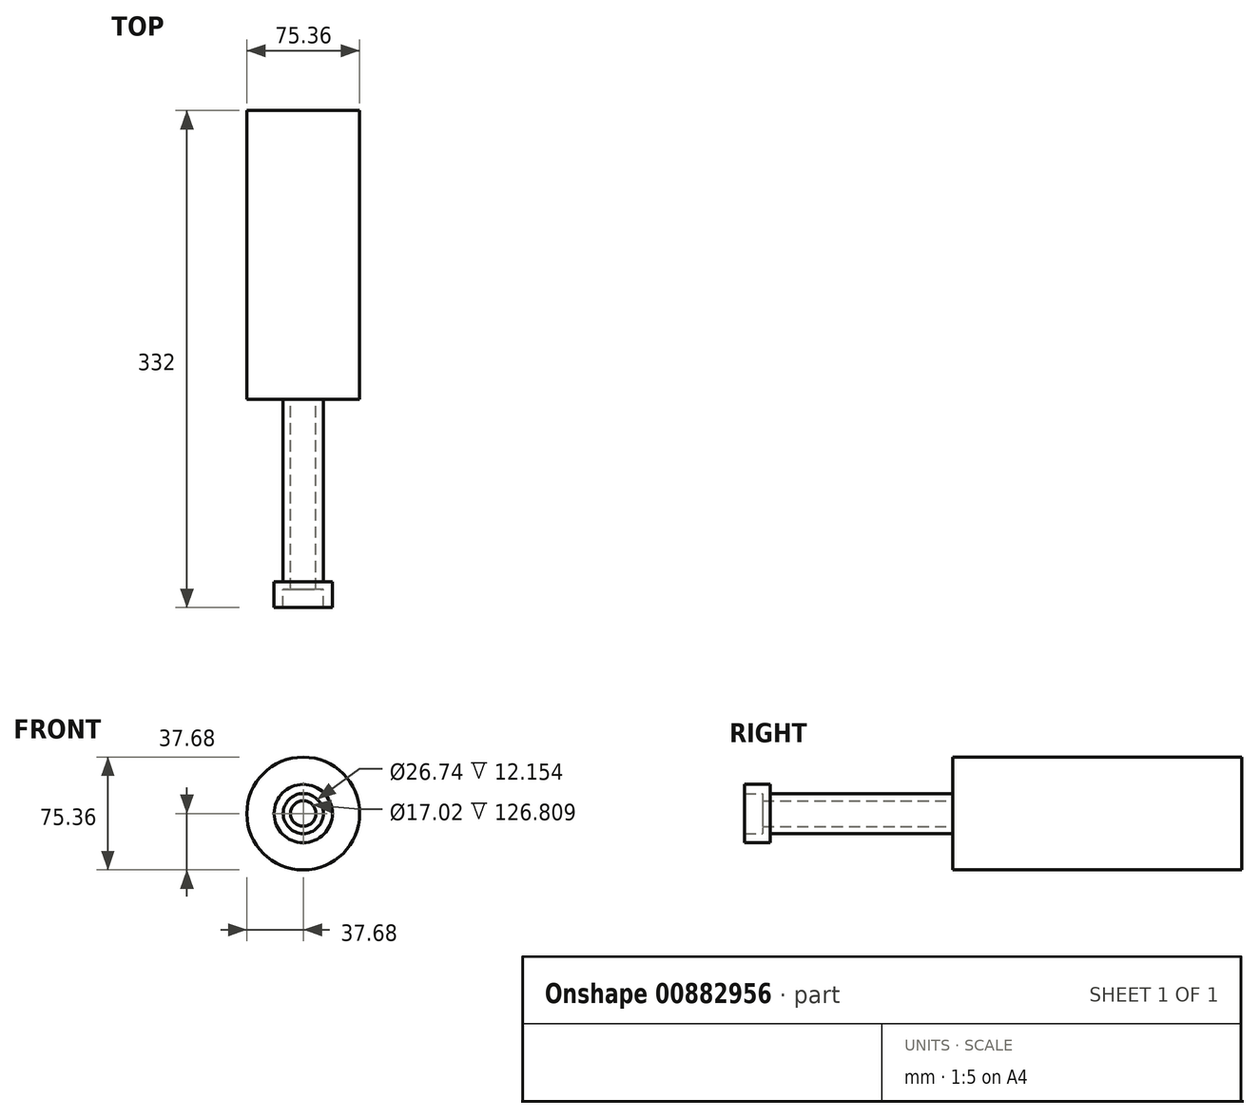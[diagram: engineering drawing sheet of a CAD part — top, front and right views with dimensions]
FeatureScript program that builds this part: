
annotation { "Feature Type Name" : "Feature", "Feature Type Description" : "" }
export const myFeature = defineFeature(function(context is Context, id is Id, definition is map)
    precondition{}
    {
        {
            var Q0;
            Q0=qCreatedBy(makeId("Right.planeOp"),FACE);
            var sketch = newSketch(context, id + "F0", { "sketchPlane" : qUnion([Q0])});
            skLineSegment(sketch, "E0.bottom", {"start": v(0, 37.68) * mm, "end": v(-193.04, 37.68) * mm});
            skLineSegment(sketch, "E0.top", {"start": v(0, 0) * mm, "end": v(-193.04, 0) * mm});
            skLineSegment(sketch, "E0.left", {"start": v(0, 37.68) * mm, "end": v(0, 0) * mm});
            skLineSegment(sketch, "E0.right", {"start": v(-193.04, 37.68) * mm, "end": v(-193.04, 0) * mm});
            skLineSegment(sketch, "E1.bottom", {"start": v(-193.04, 13.37) * mm, "end": v(-314.98, 13.37) * mm});
            skLineSegment(sketch, "E1.left", {"start": v(-193.04, 13.37) * mm, "end": v(-193.04, 0) * mm});
            skLineSegment(sketch, "E2.top", {"start": v(-314.98, 19.45) * mm, "end": v(-332, 19.45) * mm});
            skLineSegment(sketch, "E2.left", {"start": v(-314.98, 13.37) * mm, "end": v(-314.98, 19.45) * mm});
            skLineSegment(sketch, "E2.right", {"start": v(-332, 13.37) * mm, "end": v(-332, 19.45) * mm});
            skPoint(sketch, "E3.top.end.orphan", {"position": v(-314.98, 0) * mm});
            skLineSegment(sketch, "E4", {"start": v(-332, 13.37) * mm, "end": v(-319.84, 13.37) * mm});
            skLineSegment(sketch, "E5", {"start": v(-319.84, 13.37) * mm, "end": v(-319.84, 8.5) * mm});
            skLineSegment(sketch, "E6", {"start": v(-319.84, 8.5) * mm, "end": v(-193.04, 8.5) * mm});
            skLineSegment(sketch, "E7", {"start": v(-193.04, 0) * mm, "end": v(-341.72, 0) * mm, "construction": true});
            skSolve(sketch);
        }
        {
            var Q0;
            Q0=makeQuery(id+"F0.imprint","IMPRINT",FACE,{"disambiguationData":[TD([[makeQuery(id+"F0.imprint","IMPRINT",EDGE,{"derivedFrom":sQuery(id+"F0.wireOp",EDGE,"E0.bottom")}),1.0]])]});
            var Q1;
            {var subQ1=sQuery(id+"F0.wireOp",EDGE,"E1.bottom");Q1=makeQuery(id+"F0.imprint","IMPRINT",FACE,{"disambiguationData":[TD([[makeQuery(id+"F0.imprint","IMPRINT",EDGE,{"derivedFrom":subQ1}),1.0]])]});}
            var Q2;
            Q2=sQuery(id+"F0.wireOp",EDGE,"E7");
            revolve(context, id + "F1", {"surfaceOperationType" : NewSurfaceOperationType.NEW, "entities" : qUnion([Q0, Q1]), "axis" : qUnion([Q2]), "revolveType" : RevolveType.FULL});
        }
    });
